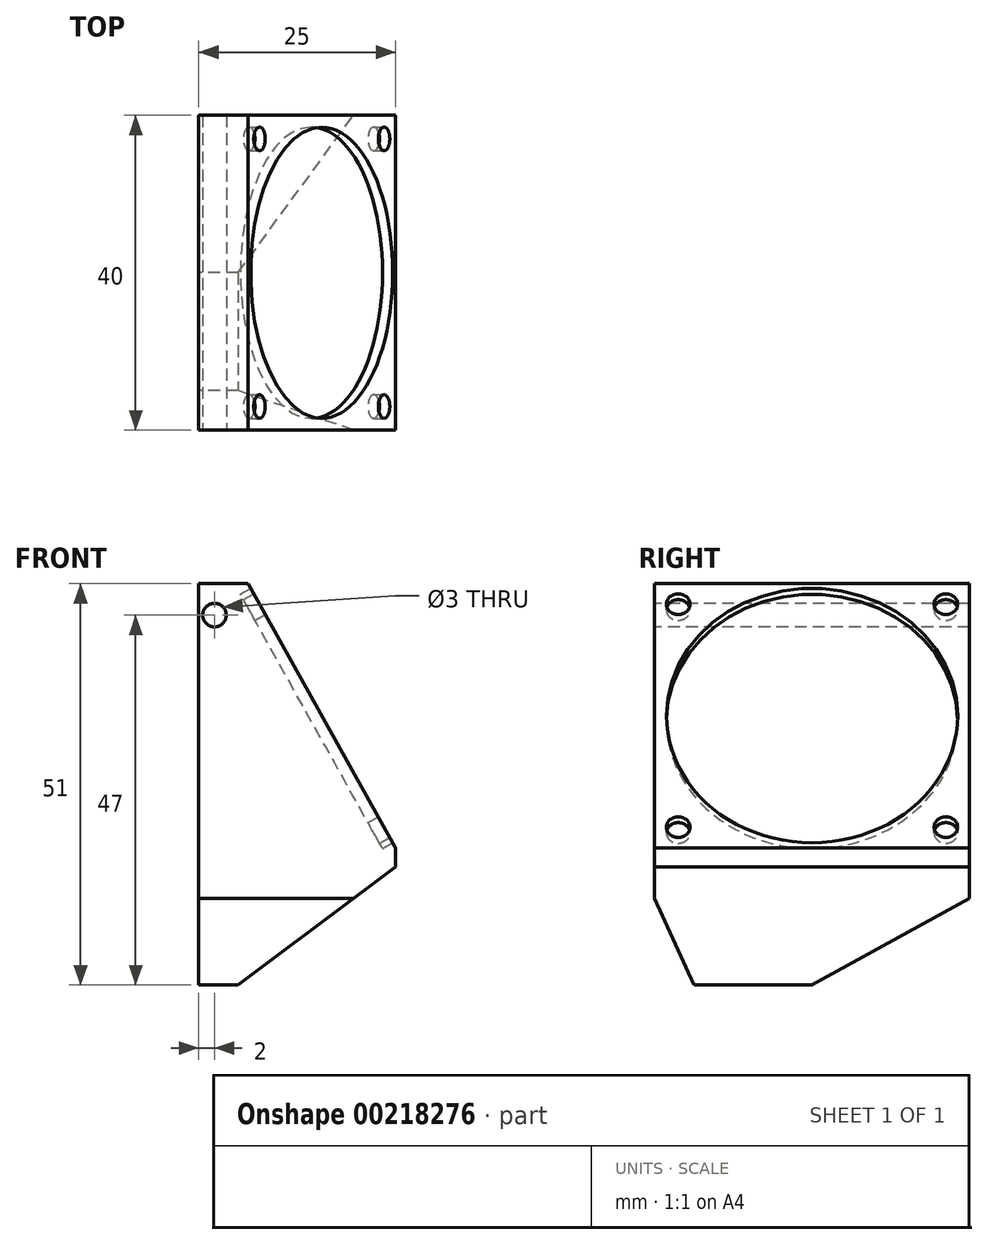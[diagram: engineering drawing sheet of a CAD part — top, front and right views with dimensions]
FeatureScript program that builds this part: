
annotation { "Feature Type Name" : "Feature", "Feature Type Description" : "" }
export const myFeature = defineFeature(function(context is Context, id is Id, definition is map)
    precondition{}
    {
        {
            var Q0;
            Q0=qCreatedBy(makeId("Right.planeOp"),FACE);
            var sketch = newSketch(context, id + "F0", { "sketchPlane" : qUnion([Q0])});
            skLineSegment(sketch, "E0.bottom", {"start": v(20, 22.76) * mm, "end": v(-20, 22.76) * mm});
            skLineSegment(sketch, "E0.top", {"start": v(0, -28.24) * mm, "end": v(-15, -28.24) * mm});
            skLineSegment(sketch, "E0.left", {"start": v(20, 22.76) * mm, "end": v(20, -17.24) * mm});
            skLineSegment(sketch, "E0.right", {"start": v(-20, 22.76) * mm, "end": v(-20, -17.24) * mm});
            skLineSegment(sketch, "E1", {"start": v(-20, -17.24) * mm, "end": v(20, -17.24) * mm});
            skLineSegment(sketch, "E2", {"start": v(-15, -24.24) * mm, "end": v(0, -24.24) * mm});
            skLineSegment(sketch, "E3", {"start": v(0, -28.24) * mm, "end": v(20, -17.24) * mm});
            skLineSegment(sketch, "E4", {"start": v(-15, -28.24) * mm, "end": v(-20, -17.24) * mm});
            skLineSegment(sketch, "E5", {"start": v(7.27, -24.24) * mm, "end": v(-16.82, -24.24) * mm});
            skSolve(sketch);
        }
        {
            var Q0;
            {var subQ4=sQuery(id+"F0.wireOp",EDGE,"E0.bottom");Q0=makeQuery(id+"F0.imprint","IMPRINT",FACE,{"disambiguationData":[TD([[makeQuery(id+"F0.imprint","IMPRINT",EDGE,{"derivedFrom":subQ4}),1.0]])]});}
            var Q1;
            {var subQ5=sQuery(id+"F0.wireOp",EDGE,"E2");Q1=makeQuery(id+"F0.imprint","IMPRINT",FACE,{"disambiguationData":[TD([[makeQuery(id+"F0.imprint","IMPRINT",EDGE,{"derivedFrom":subQ5}),1.0]])]});}
            var Q2;
            {var subQ5=sQuery(id+"F0.wireOp",EDGE,"E2");Q2=makeQuery(id+"F0.imprint","IMPRINT",FACE,{"disambiguationData":[TD([[makeQuery(id+"F0.imprint","IMPRINT",EDGE,{"derivedFrom":subQ5}),-1.0]])]});}
            extrude(context, id + "F1", {"entities" : qUnion([Q0, Q1, Q2]), "depth" : 25 * mm});
        }
        {
            var Q0;
            Q0=qCreatedBy(makeId("Front.planeOp"),FACE);
            var sketch = newSketch(context, id + "F2", { "sketchPlane" : qUnion([Q0])});
            skLineSegment(sketch, "E6", {"start": v(25, -10.8) * mm, "end": v(5, 25) * mm});
            skLineSegment(sketch, "E7", {"start": v(25, -10.8) * mm, "end": v(25, 25) * mm});
            skLineSegment(sketch, "E8", {"start": v(25, 25) * mm, "end": v(5, 25) * mm});
            skSolve(sketch);
        }
        {
            var Q0;
            Q0 = qSketchRegion(id + "F2", true);
            extrude(context, id + "F3", {"entities" : qUnion([Q0]), "operationType" : NewBodyOperationType.REMOVE, "oppositeDirection" : true, "depth" : 25 * mm, "hasSecondDirection" : true, "secondDirectionOppositeDirection" : false, "secondDirectionDepth" : 25 * mm});
        }
        {
            var Q0;
            {var subQ1=sQuery(id+"F0.wireOp",EDGE,"E1");Q0=makeQuery(id+"F0.imprint","IMPRINT",FACE,{"disambiguationData":[TD([[makeQuery(id+"F0.imprint","IMPRINT",EDGE,{"derivedFrom":subQ1}),-1.0]])]});}
            var Q1;
            {var subQ5=sQuery(id+"F0.wireOp",EDGE,"E0.top");Q1=makeQuery(id+"F0.imprint","IMPRINT",FACE,{"disambiguationData":[TD([[makeQuery(id+"F0.imprint","IMPRINT",EDGE,{"derivedFrom":subQ5}),-1.0]])]});}
            extrude(context, id + "F4", {"entities" : qUnion([Q0, Q1]), "operationType" : NewBodyOperationType.ADD, "depth" : 25 * mm});
        }
        {
            var Q0;
            Q0=makeQuery(id+"F3.boolean.opBoolean","COPY",FACE,{"derivedFrom":makeQuery(id+"F3.opExtrude","SWEPT_FACE",FACE,{"disambiguationData":[OSD([sQuery(id+"F2.wireOp",EDGE,"E6")])]})});
            var sketch = newSketch(context, id + "F5", { "sketchPlane" : qUnion([Q0])});
            skCircle(sketch, "E9", {"center": v(0, -2.38) * mm, "radius": 18.5 * mm});
            skCircle(sketch, "E10", {"center": v(-17, 13.82) * mm, "radius": 1.5 * mm});
            skCircle(sketch, "E11", {"center": v(-17, -18.62) * mm, "radius": 1.5 * mm});
            skCircle(sketch, "E12", {"center": v(17, 13.82) * mm, "radius": 1.5 * mm});
            skCircle(sketch, "E13", {"center": v(17, -18.62) * mm, "radius": 1.5 * mm});
            skSolve(sketch);
        }
        {
            var Q0;
            Q0=qCreatedBy(makeId("Front.planeOp"),FACE);
            cPlane(context, id + "F6", {"entities" : qUnion([Q0]), "cplaneType" : CPlaneType.OFFSET, "offset" : 25 * mm, "width" : 150 * mm, "height" : 150 * mm});
        }
        {
            var Q0;
            Q0=qCreatedBy(id+"F6.planeOp",FACE);
            var sketch = newSketch(context, id + "F7", { "sketchPlane" : qUnion([Q0])});
            skPoint(sketch, "E14", {"position": v(2, 18.76) * mm});
            skSolve(sketch);
        }
        {
            var Q0;
            Q0=makeQuery(id+"F4.opExtrude","CAP_EDGE",EDGE,{"disambiguationData":[OSD([sQuery(id+"F0.wireOp",EDGE,"E0.top")])],"isStart":false});
            chamfer(context, id + "F8", {"entities" : qUnion([Q0]), "chamferType" : ChamferType.TWO_OFFSETS, "width1" : 20 * mm, "oppositeDirection" : false, "width2" : 15 * mm, "tangentPropagation" : true});
        }
        {
            var Q0;
            Q0=sQuery(id+"F7.wireOp",VERTEX,"E14");
            var Q1;
            Q1=makeQuery(id+"F1.opExtrude","SWEPT_BODY",BODY,{"disambiguationData":[OSD([sQuery(id+"F0.wireOp",EDGE,"E0.bottom"),sQuery(id+"F0.wireOp",EDGE,"E0.left"),sQuery(id+"F0.wireOp",EDGE,"E0.right"),sQuery(id+"F0.wireOp",EDGE,"E1")])]});
            hole(context, id + "F9", {"style" : HoleStyle.SIMPLE, "endStyle" : HoleEndStyle.THROUGH, "holeDiameter" : 3 * mm, "isTappedThrough" : true, "tappedDepth" : 12 * mm, "tapClearance" : 3, "startFromSketch" : true, "locations" : qUnion([Q0]), "scope" : qUnion([Q1])});
        }
        {
            var Q0;
            Q0=makeQuery(id+"F5.imprint","IMPRINT",FACE,{"disambiguationData":[TD([[makeQuery(id+"F5.imprint","IMPRINT",EDGE,{"derivedFrom":sQuery(id+"F5.wireOp",EDGE,"E9")}),1.0]])]});
            var Q1;
            Q1=makeQuery(id+"F5.imprint","IMPRINT",FACE,{"disambiguationData":[TD([[makeQuery(id+"F5.imprint","IMPRINT",EDGE,{"derivedFrom":sQuery(id+"F5.wireOp",EDGE,"E11")}),1.0]])]});
            var Q2;
            Q2=makeQuery(id+"F5.imprint","IMPRINT",FACE,{"disambiguationData":[TD([[makeQuery(id+"F5.imprint","IMPRINT",EDGE,{"derivedFrom":sQuery(id+"F5.wireOp",EDGE,"E13")}),1.0]])]});
            var Q3;
            Q3=makeQuery(id+"F5.imprint","IMPRINT",FACE,{"disambiguationData":[TD([[makeQuery(id+"F5.imprint","IMPRINT",EDGE,{"derivedFrom":sQuery(id+"F5.wireOp",EDGE,"E10")}),1.0]])]});
            var Q4;
            Q4=makeQuery(id+"F5.imprint","IMPRINT",FACE,{"disambiguationData":[TD([[makeQuery(id+"F5.imprint","IMPRINT",EDGE,{"derivedFrom":sQuery(id+"F5.wireOp",EDGE,"E12")}),1.0]])]});
            extrude(context, id + "F10", {"entities" : qUnion([Q0, Q1, Q2, Q3, Q4]), "operationType" : NewBodyOperationType.REMOVE, "oppositeDirection" : true, "depth" : 1.5 * mm});
        }
    });
